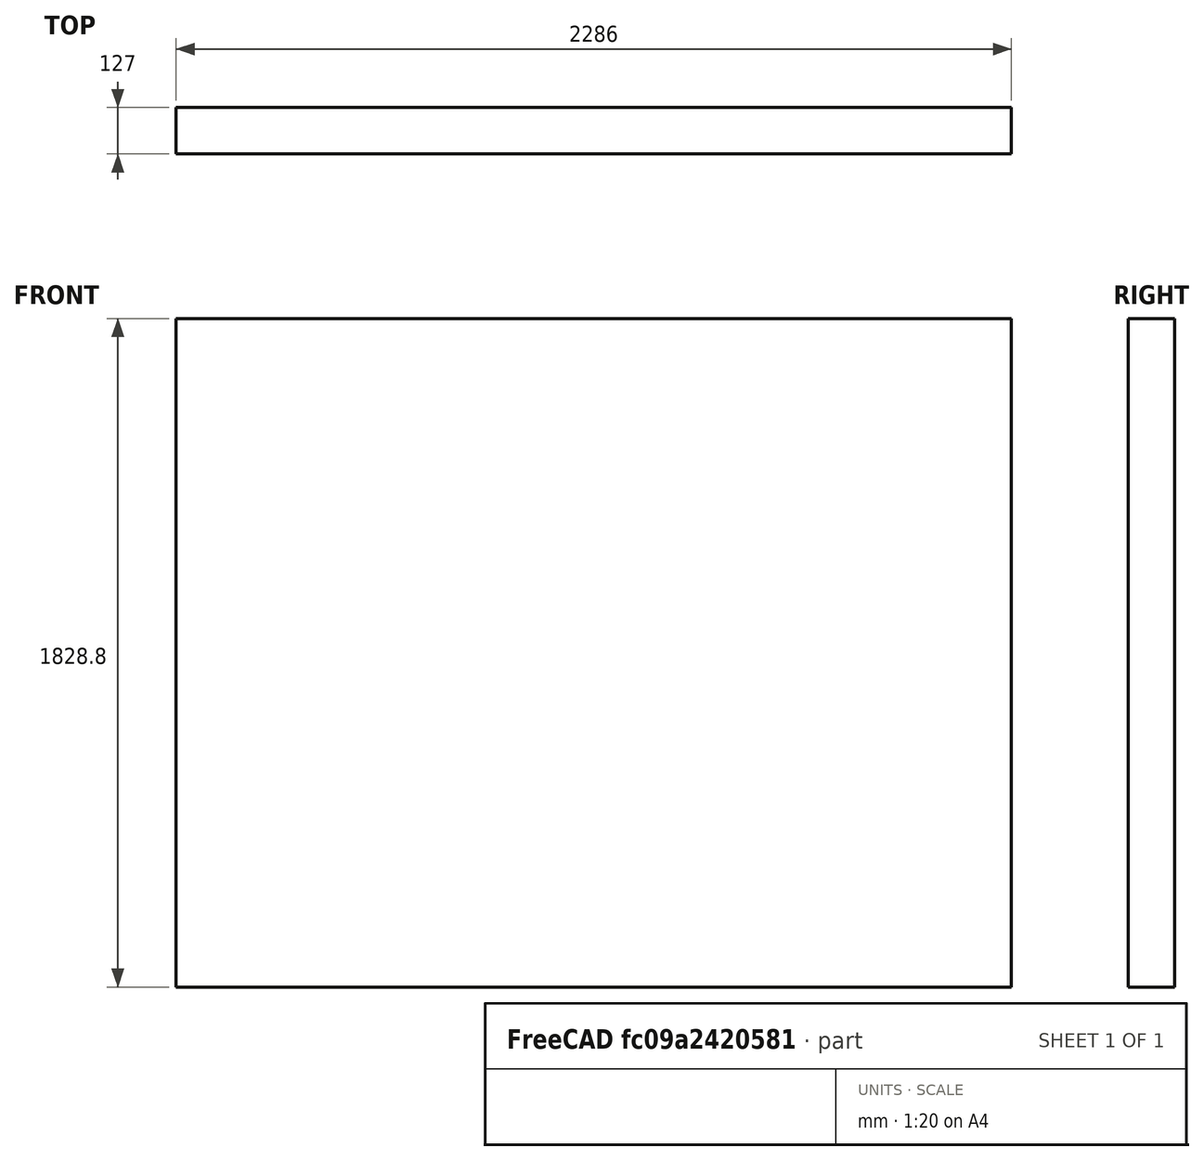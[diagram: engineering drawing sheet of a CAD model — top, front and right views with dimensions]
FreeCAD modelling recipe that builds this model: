
FCSTD DOCUMENT  (FreeCAD 0.20R29177 (Git))
Label: FenceSection
License: All rights reserved
LicenseURL: http://en.wikipedia.org/wiki/All_rights_reserved
objects: Sketcher::SketchObject×1, PartDesign::Pad×1, PartDesign::Body×1
note: 4 computed .brp shape members not serialized (recipe doc carries the construction recipe); baked Part::Feature solids carry a one-line shape summary decoded from their .brp

FEATURE [Sketcher::SketchObject] Sketch
  FullyConstrained = true
  MapMode = 5
  Support = -> [XY_Plane]
  sketch-geometry (4):
    g0: LineSegment StartX=0 StartY=0 StartZ=0 EndX=2286 EndY=0 EndZ=0
    g1: LineSegment StartX=2286 StartY=0 StartZ=0 EndX=2286 EndY=127 EndZ=0
    g2: LineSegment StartX=2286 StartY=127 StartZ=0 EndX=0 EndY=127 EndZ=0
    g3: LineSegment StartX=0 StartY=127 StartZ=0 EndX=0 EndY=0 EndZ=0
  constraints (11):
    c: Coincident(g0,g1)
    c: Coincident(g1,g2)
    c: Coincident(g2,g3)
    c: Coincident(g3,g0)
    c: Horizontal(g0)
    c: Horizontal(g2)
    c: Vertical(g1)
    c: Vertical(g3)
    c: Coincident(g0,g-1)
    c: DistanceX(g0,g0) = 2286
    c: DistanceY(g3,g3) = 127
FEATURE [PartDesign::Pad] Pad
  Direction = (0,0,1)
  Length = 1828.8
  Length2 = 10
  Profile = -> Sketch
  ReferenceAxis = -> Sketch [N_Axis]
  Type = 0
FEATURE [PartDesign::Body] Body
  Group = -> [Sketch,Pad]
  Origin = -> Origin
  Tip = -> Pad
